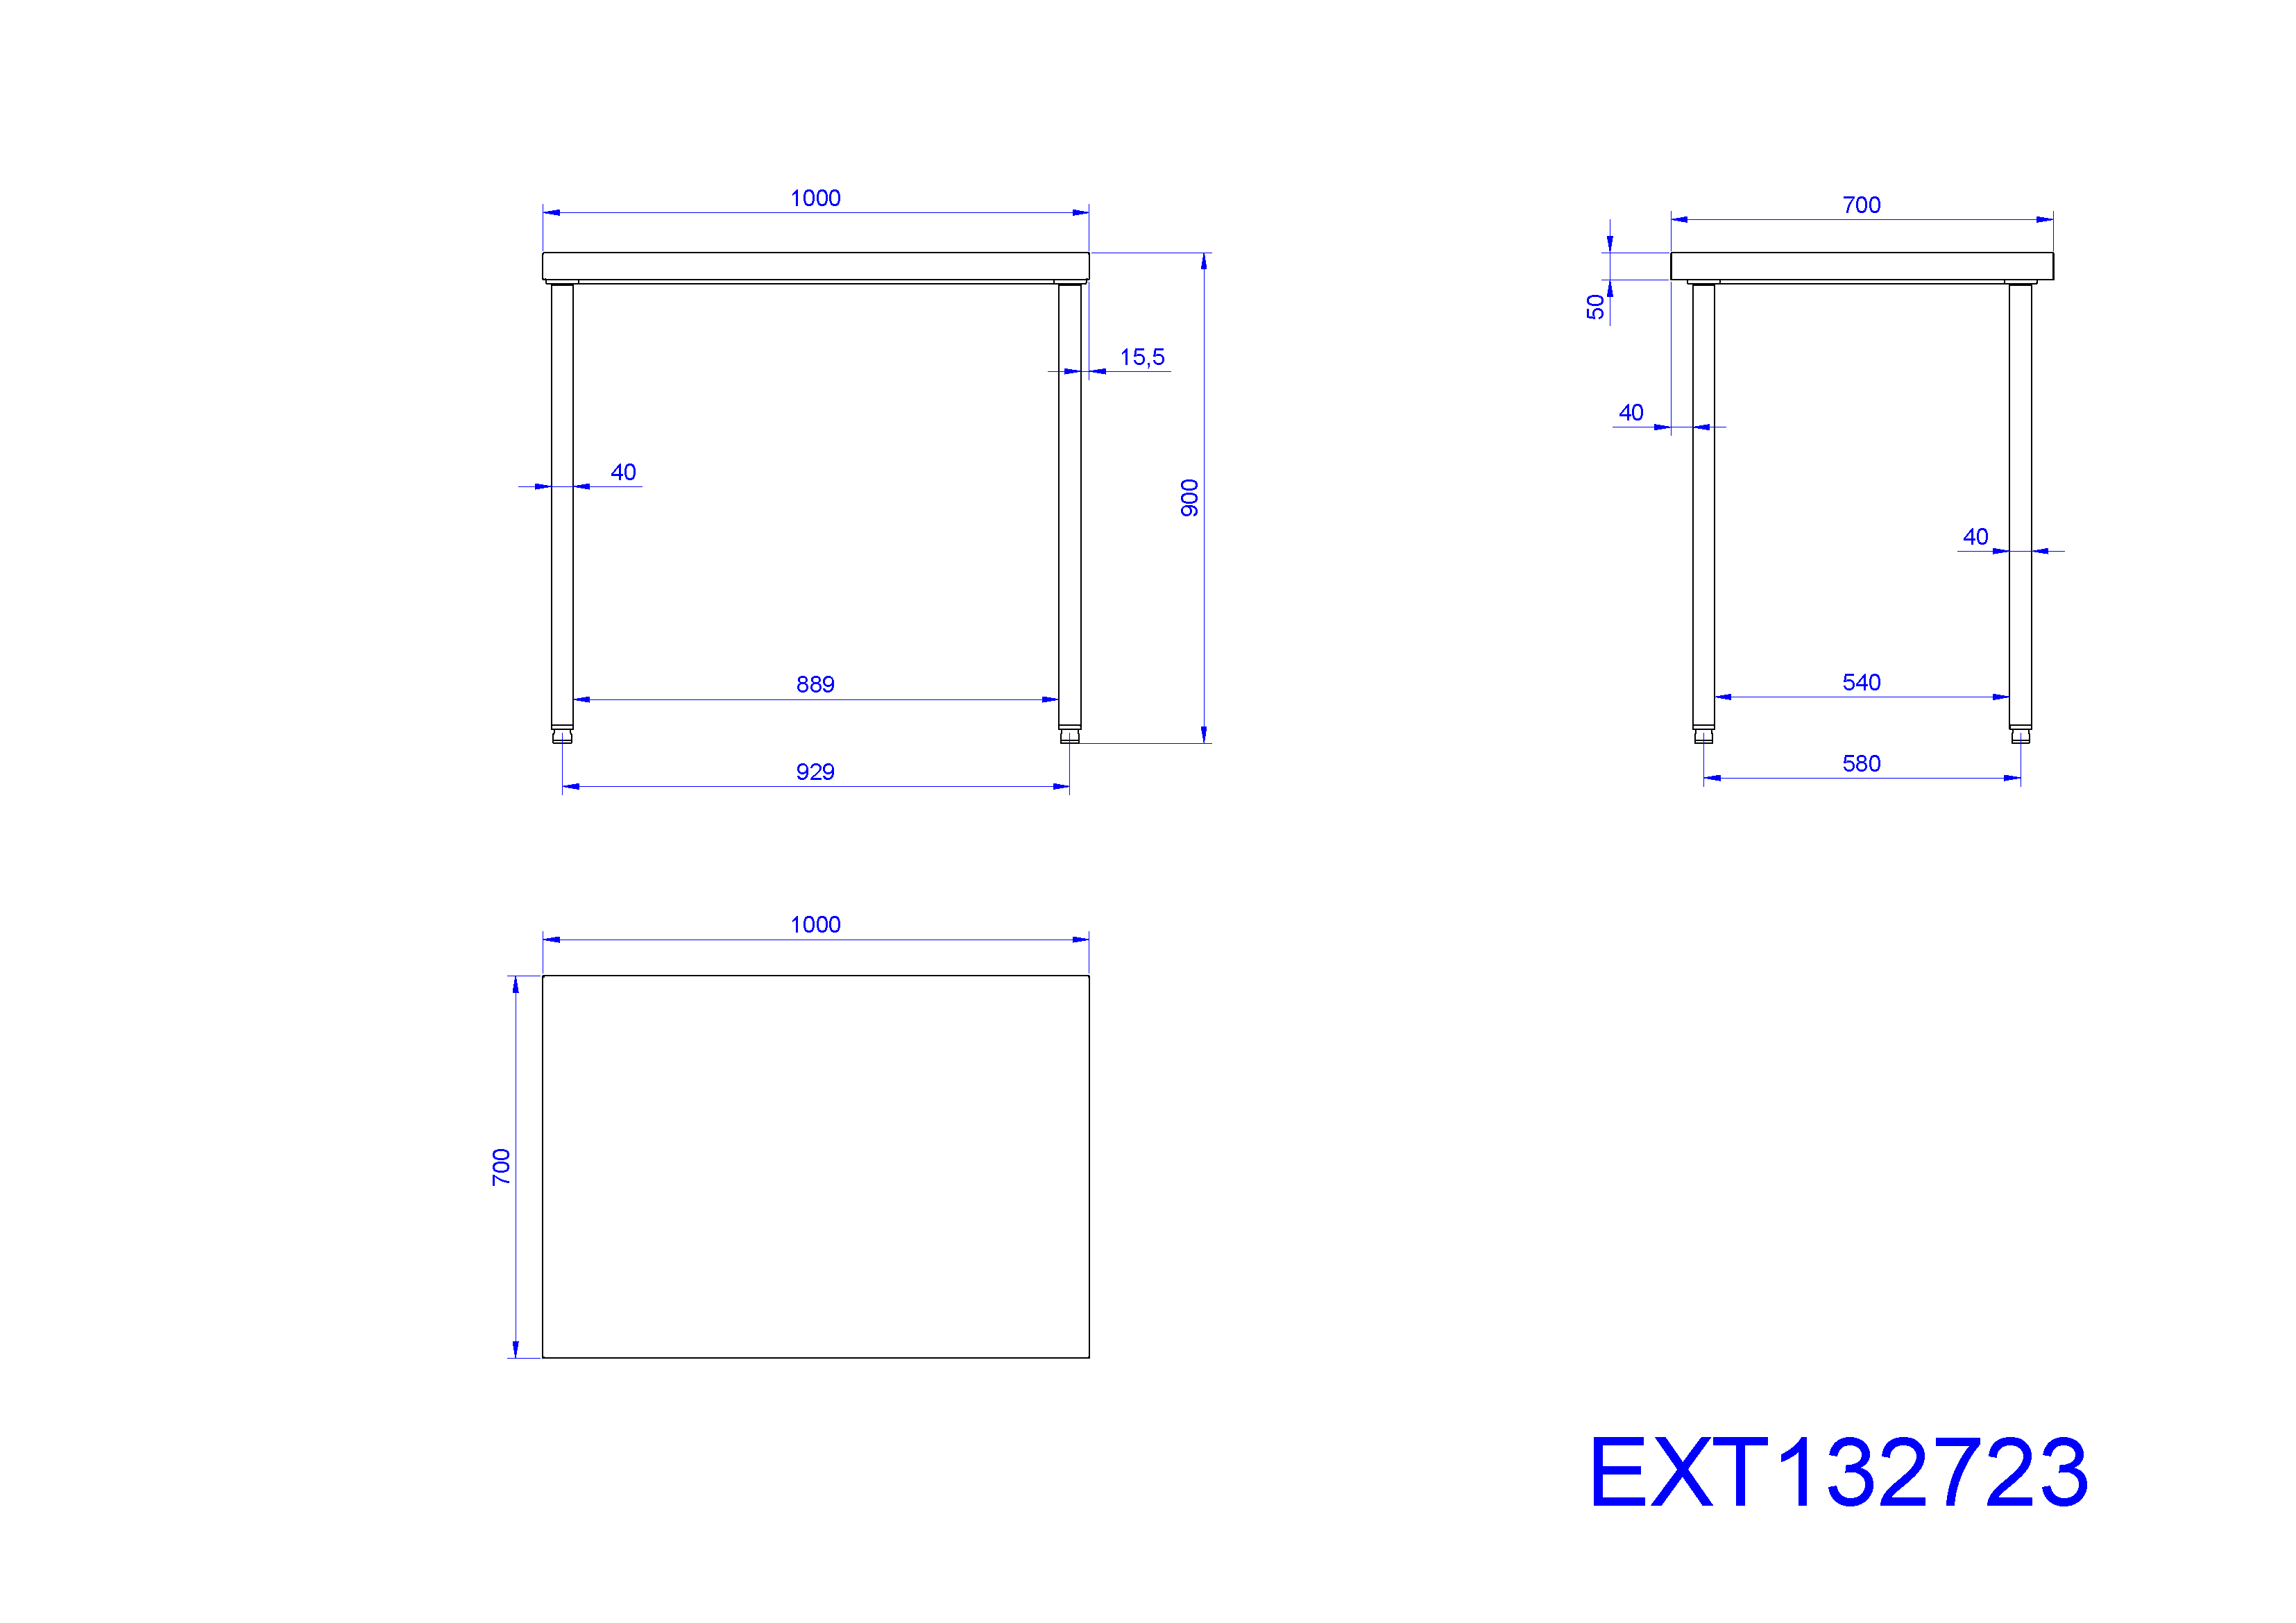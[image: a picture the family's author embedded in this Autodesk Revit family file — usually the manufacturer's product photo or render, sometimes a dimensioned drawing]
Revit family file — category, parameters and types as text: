
# Revit family: QF_ZANUSSI_132844_WTD2007N
name_source: partatom
category: Attrezzature speciali
units: mm (PartAtom-declared; Revit-internal decimal feet)

## family parameters
Basato su piano di lavoro = No
Condiviso = No
Punto di calcolo locali = No
Quota connettore circolare = Usa diametro
Sempre verticale = Sì
Taglio con vuoti quando caricato = No
Tipo di parte = Normale

## types (1)
- Standard
    Accessory = Sì
    Cold Water Size = 0 mm
    Compressed Air Pressure = 0.0 Pa
    Compressed Air Size = 0 mm
    Compressed Air Volume = 0.0 L/s
    Condensate Return Size = 0 mm
    Cycle = 0 Hz
    Depth Actual = 700 mm  [stored 2.29659 ft]
    Descrizione = WORK TABLE-DISASSEMBLED 2000MM
    Direct Waste Size = 0 mm
    Gas Input Pressure = 0
    Gas KW = 0
    Gas Size = 0 mm
    HP = 0 HP
    Height Actual = 900 mm  [stored 2.95276 ft]
    Hot Water Size = 0 mm
    Item Number = 132844
    Length Actual = 2000 mm  [stored 6.56168 ft]
    Modello = WTD2007N
    Phase = 0
    Produttore = Zanussi
    Prospetto di default = 0 mm  [stored 0 ft]
    Refrigerant Compressor Remote = Sì
    Refrigeration Liquid Line Size = 0 mm  [stored 0 ft]
    Refrigeration Suction Line Size = 0 mm  [stored 0 ft]
    Steam Consumption per Hour = 0
    Steam Supply Maximum Pressure = 0.0 Pa
    Steam Supply Minimum Pressure = 0.0 Pa
    Steam Supply Size = 0 mm
    URL = http://www.zanussiprofessional.com
    URL Manufacturer = http://www.zanussiprofessional.com
    Volts = 0 V
    Watts = 0 W
    Weight = 63.00 kg

note: source unit labels omitted for Gas Input Pressure — the stored unit's dimension contradicts the parameter name (converter mislabeling)

note: [stored X ft] marks values corroborated as IEEE doubles in the binary element streams (Revit-internal decimal feet)

## geometry (parser evidence)
native form markers: Sweep x2
no freeform markers — native parametric forms only
